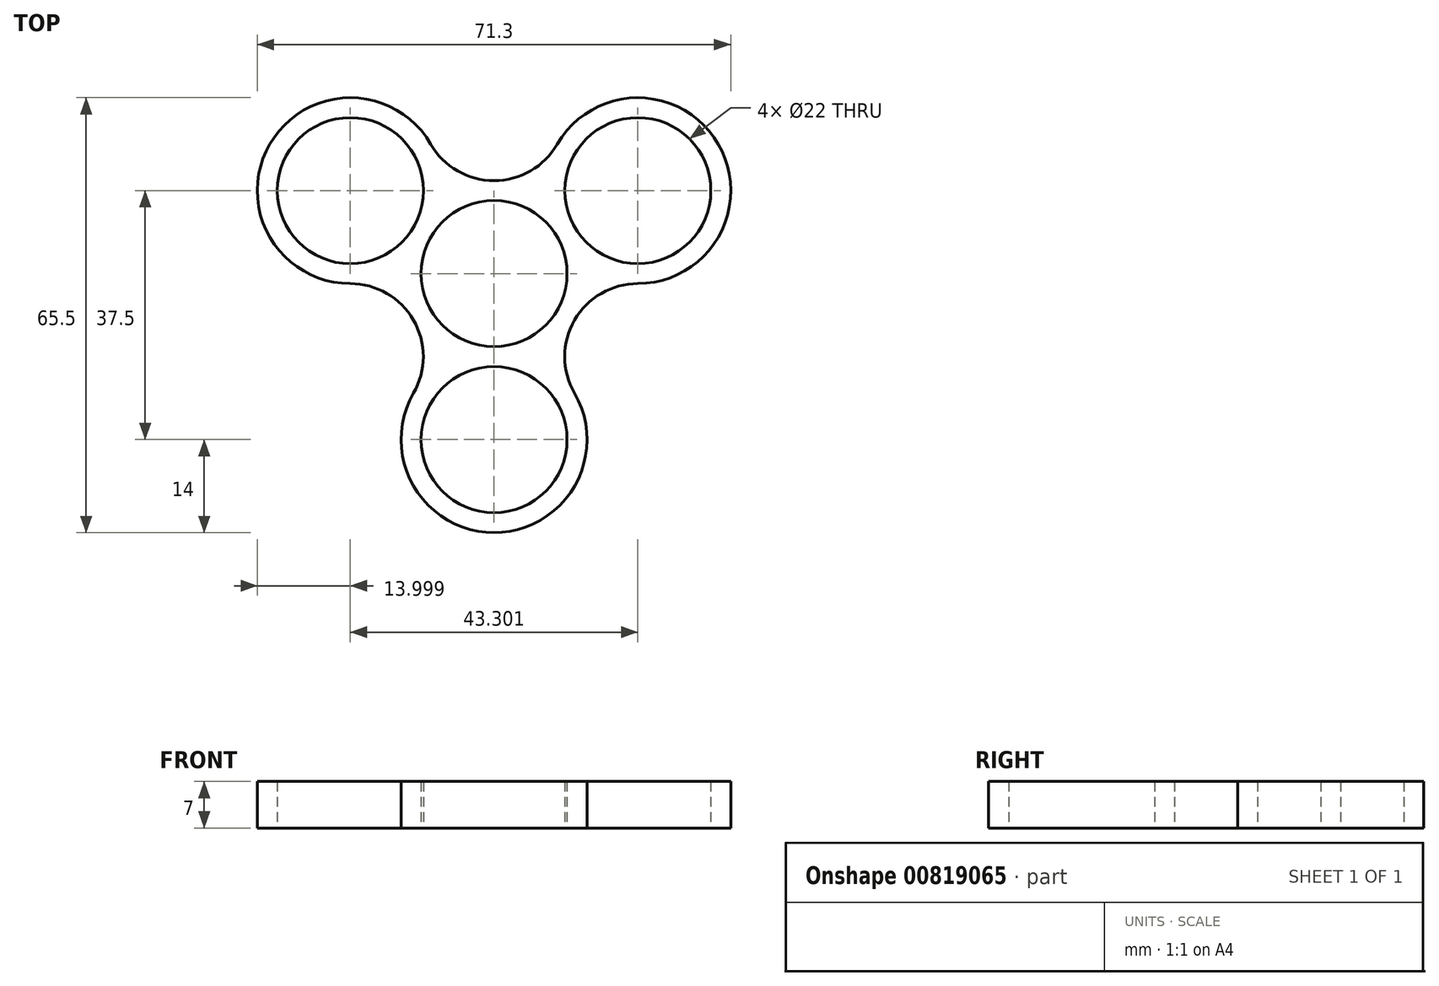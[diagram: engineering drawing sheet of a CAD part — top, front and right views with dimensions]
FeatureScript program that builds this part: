
annotation { "Feature Type Name" : "Feature", "Feature Type Description" : "" }
export const myFeature = defineFeature(function(context is Context, id is Id, definition is map)
    precondition{}
    {
        {
            var Q0;
            Q0=qCreatedBy(makeId("Top.planeOp"),FACE);
            var sketch = newSketch(context, id + "F0", { "sketchPlane" : qUnion([Q0])});
            skCircle(sketch, "E0", {"center": v(0, 0) * mm, "radius": 11 * mm});
            skCircle(sketch, "E1", {"center": v(0, 0) * mm, "radius": 25 * mm});
            skCircle(sketch, "E2", {"center": v(0, 0) * mm, "radius": 39 * mm});
            skCircle(sketch, "E3", {"center": v(0, -25) * mm, "radius": 11 * mm});
            skCircle(sketch, "E4", {"center": v(0, -25) * mm, "radius": 14 * mm});
            skCircle(sketch, "E5.1.0", {"center": v(21.65, -12.5) * mm, "radius": 11 * mm});
            skCircle(sketch, "E5.2.0", {"center": v(21.65, 12.5) * mm, "radius": 11 * mm});
            skCircle(sketch, "E5.3.0", {"center": v(0, 25) * mm, "radius": 11 * mm});
            skCircle(sketch, "E5.4.0", {"center": v(-21.65, 12.5) * mm, "radius": 11 * mm});
            skCircle(sketch, "E5.5.0", {"center": v(-21.65, -12.5) * mm, "radius": 11 * mm});
            skCircle(sketch, "E6", {"center": v(21.65, 12.5) * mm, "radius": 14 * mm});
            skCircle(sketch, "E7", {"center": v(-21.65, 12.5) * mm, "radius": 14 * mm});
            skSolve(sketch);
        }
        {
            var Q0;
            {var subQ0=sQuery(id+"F0.wireOp",EDGE,"bxVbq05q-Kk38-YU8Z-T1T8-1F7UuoJj0hau");var subQ1=sQuery(id+"F0.wireOp",EDGE,"E1");var subQ2=makeQuery(id+"F0.imprint","INTERSECT",VERTEX,{"disambiguationData":[OD(0.0)],"derivedFrom":[subQ1,subQ0]});Q0=makeQuery(id+"F0.imprint","IMPRINT",FACE,{"disambiguationData":[TD([[makeQuery(id+"F0.imprint","IMPRINT",EDGE,{"disambiguationData":[TD([[subQ2,-1.0]])],"derivedFrom":subQ1}),1.0]])]});}
            var Q1;
            {var subQ0=sQuery(id+"F0.wireOp",EDGE,"E4");var subQ1=sQuery(id+"F0.wireOp",EDGE,"E1");var subQ8=makeQuery(id+"F0.imprint","INTERSECT",VERTEX,{"disambiguationData":[OD(0.0)],"derivedFrom":[subQ1,subQ0]});Q1=makeQuery(id+"F0.imprint","IMPRINT",FACE,{"disambiguationData":[TD([[makeQuery(id+"F0.imprint","IMPRINT",EDGE,{"disambiguationData":[TD([[subQ8,-1.0]])],"derivedFrom":subQ1}),1.0]])]});}
            var Q2;
            {var subQ0=sQuery(id+"F0.wireOp",EDGE,"E4");var subQ2=sQuery(id+"F0.wireOp",EDGE,"E1");var subQ3=makeQuery(id+"F0.imprint","INTERSECT",VERTEX,{"disambiguationData":[OD(0.0)],"derivedFrom":[subQ2,subQ0]});Q2=makeQuery(id+"F0.imprint","IMPRINT",FACE,{"disambiguationData":[TD([[makeQuery(id+"F0.imprint","IMPRINT",EDGE,{"disambiguationData":[TD([[subQ3,-1.0]])],"derivedFrom":subQ2}),-1.0]])]});}
            var Q3;
            {var subQ0=sQuery(id+"F0.wireOp",EDGE,"E5.2.0");var subQ1=sQuery(id+"F0.wireOp",EDGE,"E1");var subQ2=makeQuery(id+"F0.imprint","INTERSECT",VERTEX,{"disambiguationData":[OD(0.0)],"derivedFrom":[subQ1,subQ0]});Q3=makeQuery(id+"F0.imprint","IMPRINT",FACE,{"disambiguationData":[TD([[makeQuery(id+"F0.imprint","IMPRINT",EDGE,{"disambiguationData":[TD([[subQ2,-1.0]])],"derivedFrom":subQ1}),1.0]])]});}
            var Q4;
            {var subQ2=sQuery(id+"F0.wireOp",EDGE,"E1");var subQ4=sQuery(id+"F0.wireOp",EDGE,"E5.2.0");var subQ5=makeQuery(id+"F0.imprint","INTERSECT",VERTEX,{"disambiguationData":[OD(0.0)],"derivedFrom":[subQ2,subQ4]});Q4=makeQuery(id+"F0.imprint","IMPRINT",FACE,{"disambiguationData":[TD([[makeQuery(id+"F0.imprint","IMPRINT",EDGE,{"disambiguationData":[TD([[subQ5,-1.0]])],"derivedFrom":subQ2}),-1.0]])]});}
            var Q5;
            {var subQ0=sQuery(id+"F0.wireOp",EDGE,"bxVbq05q-Kk38-YU8Z-T1T8-1F7UuoJj0hau");var subQ2=sQuery(id+"F0.wireOp",EDGE,"E1");var subQ3=makeQuery(id+"F0.imprint","INTERSECT",VERTEX,{"disambiguationData":[OD(0.0)],"derivedFrom":[subQ2,subQ0]});Q5=makeQuery(id+"F0.imprint","IMPRINT",FACE,{"disambiguationData":[TD([[makeQuery(id+"F0.imprint","IMPRINT",EDGE,{"disambiguationData":[TD([[subQ3,-1.0]])],"derivedFrom":subQ2}),-1.0]])]});}
            var Q6;
            {var subQ7=sQuery(id+"F0.wireOp",EDGE,"E6");var subQ12=sQuery(id+"F0.wireOp",EDGE,"E0");var subQ13=makeQuery(id+"F0.imprint","INTERSECT",VERTEX,{"derivedFrom":[subQ12,subQ7]});Q6=makeQuery(id+"F0.imprint","IMPRINT",FACE,{"disambiguationData":[TD([[makeQuery(id+"F0.imprint","IMPRINT",EDGE,{"disambiguationData":[TD([[subQ13,1.0]])],"derivedFrom":subQ12}),-1.0]])]});}
            var Q7;
            {var subQ4=sQuery(id+"F0.wireOp",EDGE,"E6");var subQ5=sQuery(id+"F0.wireOp",EDGE,"E0");var subQ6=makeQuery(id+"F0.imprint","INTERSECT",VERTEX,{"derivedFrom":[subQ5,subQ4]});Q7=makeQuery(id+"F0.imprint","IMPRINT",FACE,{"disambiguationData":[TD([[makeQuery(id+"F0.imprint","IMPRINT",EDGE,{"disambiguationData":[TD([[subQ6,-1.0]])],"derivedFrom":subQ5}),-1.0]])]});}
            var Q8;
            {var subQ4=sQuery(id+"F0.wireOp",EDGE,"E7");var subQ8=sQuery(id+"F0.wireOp",EDGE,"E0");var subQ9=makeQuery(id+"F0.imprint","INTERSECT",VERTEX,{"disambiguationData":[OD(0.0)],"derivedFrom":[subQ8,subQ4]});Q8=makeQuery(id+"F0.imprint","IMPRINT",FACE,{"disambiguationData":[TD([[makeQuery(id+"F0.imprint","IMPRINT",EDGE,{"disambiguationData":[TD([[subQ9,-1.0]])],"derivedFrom":subQ8}),-1.0]])]});}
            var Q9;
            {var subQ0=sQuery(id+"F0.wireOp",EDGE,"E7");var subQ1=sQuery(id+"F0.wireOp",EDGE,"E1");var subQ2=makeQuery(id+"F0.imprint","INTERSECT",VERTEX,{"disambiguationData":[OD(0.0)],"derivedFrom":[subQ1,subQ0]});Q9=makeQuery(id+"F0.imprint","IMPRINT",FACE,{"disambiguationData":[TD([[makeQuery(id+"F0.imprint","IMPRINT",EDGE,{"disambiguationData":[TD([[subQ2,-1.0]])],"derivedFrom":subQ1}),-1.0]])]});}
            var Q10;
            {var subQ0=sQuery(id+"F0.wireOp",EDGE,"E7");var subQ1=sQuery(id+"F0.wireOp",EDGE,"E1");var subQ2=makeQuery(id+"F0.imprint","INTERSECT",VERTEX,{"disambiguationData":[OD(0.0)],"derivedFrom":[subQ1,subQ0]});Q10=makeQuery(id+"F0.imprint","IMPRINT",FACE,{"disambiguationData":[TD([[makeQuery(id+"F0.imprint","IMPRINT",EDGE,{"disambiguationData":[TD([[subQ2,-1.0]])],"derivedFrom":subQ1}),1.0]])]});}
            extrude(context, id + "F1", {"entities" : qUnion([Q0, Q1, Q2, Q3, Q4, Q5, Q6, Q7, Q8, Q9, Q10]), "depth" : 7 * mm, "offsetDistance" : 25 * mm});
        }
    });
